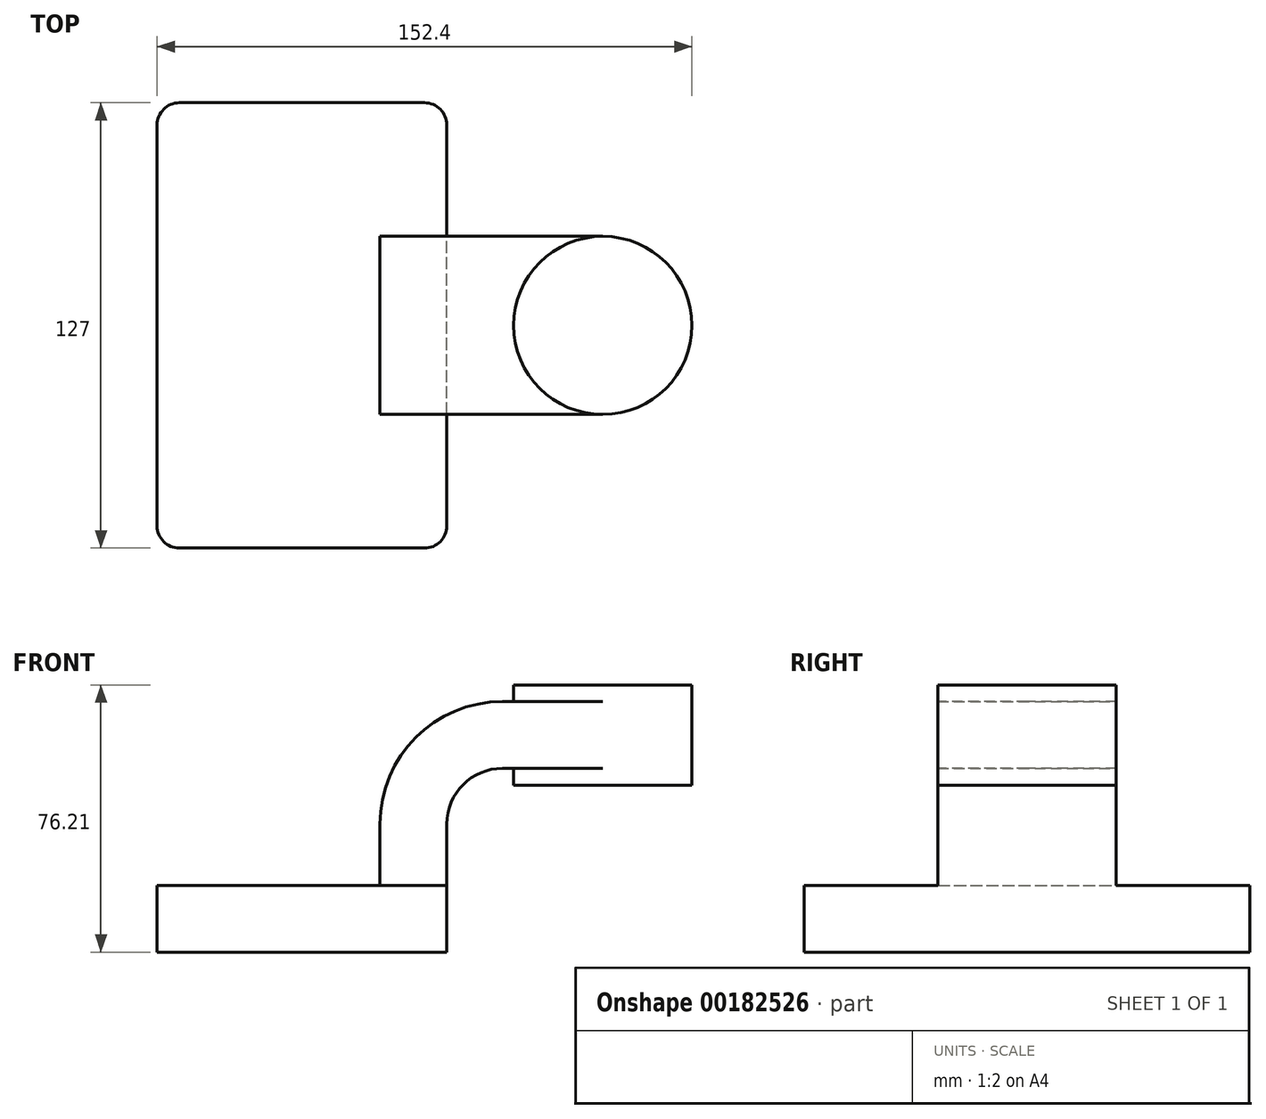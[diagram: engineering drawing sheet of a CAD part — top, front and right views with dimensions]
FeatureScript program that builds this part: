
annotation { "Feature Type Name" : "Feature", "Feature Type Description" : "" }
export const myFeature = defineFeature(function(context is Context, id is Id, definition is map)
    precondition{}
    {
        {
            var Q0;
            Q0=qCreatedBy(makeId("Front.planeOp"),FACE);
            var sketch = newSketch(context, id + "F0", { "sketchPlane" : qUnion([Q0])});
            skLineSegment(sketch, "E0.bottom", {"start": v(-41.28, 9.52) * mm, "end": v(41.27, 9.53) * mm});
            skLineSegment(sketch, "E0.top", {"start": v(-41.28, -9.53) * mm, "end": v(41.28, -9.53) * mm});
            skLineSegment(sketch, "E0.left", {"start": v(-41.28, 9.52) * mm, "end": v(-41.27, -9.53) * mm});
            skLineSegment(sketch, "E0.right", {"start": v(41.28, 9.53) * mm, "end": v(41.28, -9.52) * mm});
            skPoint(sketch, "E0.middle", {"position": v(0, 0) * mm});
            skLineSegment(sketch, "E1.bottom", {"start": v(60.32, 66.67) * mm, "end": v(111.12, 66.67) * mm});
            skLineSegment(sketch, "E1.top", {"start": v(60.32, 38.1) * mm, "end": v(111.12, 38.1) * mm});
            skLineSegment(sketch, "E1.left", {"start": v(60.32, 66.67) * mm, "end": v(60.32, 38.1) * mm});
            skLineSegment(sketch, "E1.right", {"start": v(111.12, 66.67) * mm, "end": v(111.12, 38.1) * mm});
            skPoint(sketch, "E1.middle", {"position": v(85.73, 52.39) * mm});
            skLineSegment(sketch, "E2", {"start": v(41.27, 9.53) * mm, "end": v(41.27, 27) * mm});
            skArc(sketch, "E3", {"start": v(41.28, 27) * mm, "mid": v(45.92, 38.23) * mm, "end": v(57.15, 42.88) * mm});
            skLineSegment(sketch, "E4", {"start": v(57.15, 42.88) * mm, "end": v(85.72, 42.88) * mm});
            skLineSegment(sketch, "E5.0", {"start": v(57.15, 61.93) * mm, "end": v(85.73, 61.93) * mm});
            skArc(sketch, "E5.1", {"start": v(22.23, 27) * mm, "mid": v(32.45, 51.7) * mm, "end": v(57.15, 61.93) * mm});
            skLineSegment(sketch, "E5.2", {"start": v(22.22, 9.53) * mm, "end": v(22.22, 27) * mm});
            skFitSpline(sketch, "E6", {"points": [v(-41.28, 9.53) * mm, v(57.15, 61.93) * mm], "startDerivative": vector(3.4, 88.06) * mm, "endDerivative": vector(160.5, -5.82) * mm});
            skPoint(sketch, "E7", {"position": v(85.72, 38.1) * mm});
            skLineSegment(sketch, "E8", {"start": v(85.72, 38.1) * mm, "end": v(85.72, 66.67) * mm});
            skSolve(sketch);
        }
        {
            var Q0;
            Q0=makeQuery(id+"F0.imprint","IMPRINT",FACE,{"disambiguationData":[TD([[makeQuery(id+"F0.imprint","IMPRINT",EDGE,{"derivedFrom":sQuery(id+"F0.wireOp",EDGE,"E0.top")}),1.0]])]});
            extrude(context, id + "F1", {"entities" : qUnion([Q0]), "endBound" : BoundingType.SYMMETRIC, "depth" : 127 * mm});
        }
        {
            var Q0;
            {var subQ1=sQuery(id+"F0.wireOp",EDGE,"E2");Q0=makeQuery(id+"F0.imprint","IMPRINT",FACE,{"disambiguationData":[TD([[makeQuery(id+"F0.imprint","IMPRINT",EDGE,{"derivedFrom":subQ1}),1.0]])]});}
            var Q1;
            {var subQ0=sQuery(id+"F0.wireOp",EDGE,"E5.0");var subQ1=sQuery(id+"F0.wireOp",EDGE,"E1.left");var subQ2=makeQuery(id+"F0.imprint","INTERSECT",VERTEX,{"derivedFrom":[subQ1,subQ0]});Q1=makeQuery(id+"F0.imprint","IMPRINT",FACE,{"disambiguationData":[TD([[makeQuery(id+"F0.imprint","IMPRINT",EDGE,{"disambiguationData":[TD([[subQ2,-1.0]])],"derivedFrom":subQ1}),1.0]])]});}
            extrude(context, id + "F2", {"entities" : qUnion([Q0, Q1]), "operationType" : NewBodyOperationType.ADD, "endBound" : BoundingType.SYMMETRIC, "depth" : 50.8 * mm});
        }
        {
            var Q0;
            Q0=makeQuery(id+"F0.imprint","IMPRINT",FACE,{"disambiguationData":[TD([[makeQuery(id+"F0.imprint","IMPRINT",EDGE,{"derivedFrom":sQuery(id+"F0.wireOp",EDGE,"E5.1")}),1.0]])]});
            extrude(context, id + "F3", {"entities" : qUnion([Q0]), "operationType" : NewBodyOperationType.ADD, "endBound" : BoundingType.SYMMETRIC, "depth" : 15.88 * mm});
        }
        {
            var Q0;
            Q0=makeQuery(id+"F1.opExtrude","CAP_EDGE",EDGE,{"disambiguationData":[OSD([sQuery(id+"F0.wireOp",EDGE,"E0.left")])],"isStart":false});
            var Q1;
            Q1=makeQuery(id+"F1.opExtrude","CAP_EDGE",EDGE,{"disambiguationData":[OSD([sQuery(id+"F0.wireOp",EDGE,"E0.right")])],"isStart":false});
            var Q2;
            Q2=makeQuery(id+"F1.opExtrude","CAP_EDGE",EDGE,{"disambiguationData":[OSD([sQuery(id+"F0.wireOp",EDGE,"E0.right")])],"isStart":true});
            var Q3;
            Q3=makeQuery(id+"F1.opExtrude","CAP_EDGE",EDGE,{"disambiguationData":[OSD([sQuery(id+"F0.wireOp",EDGE,"E0.left")])],"isStart":true});
            fillet(context, id + "F4", {"entities" : qUnion([Q0, Q1, Q2, Q3]), "radius" : 6.35 * mm, "tangentPropagation" : true, "allowEdgeOverflow" : false});
        }
        {
            var Q0;
            {var subQ0=sQuery(id+"F0.wireOp",EDGE,"E1.right");Q0=makeQuery(id+"F0.imprint","IMPRINT",FACE,{"disambiguationData":[TD([[makeQuery(id+"F0.imprint","IMPRINT",EDGE,{"derivedFrom":subQ0}),-1.0]])]});}
            var Q1;
            Q1=sQuery(id+"F0.wireOp",EDGE,"E8");
            revolve(context, id + "F5", {"operationType" : NewBodyOperationType.ADD, "entities" : qUnion([Q0]), "axis" : qUnion([Q1]), "revolveType" : RevolveType.FULL});
        }
    });
